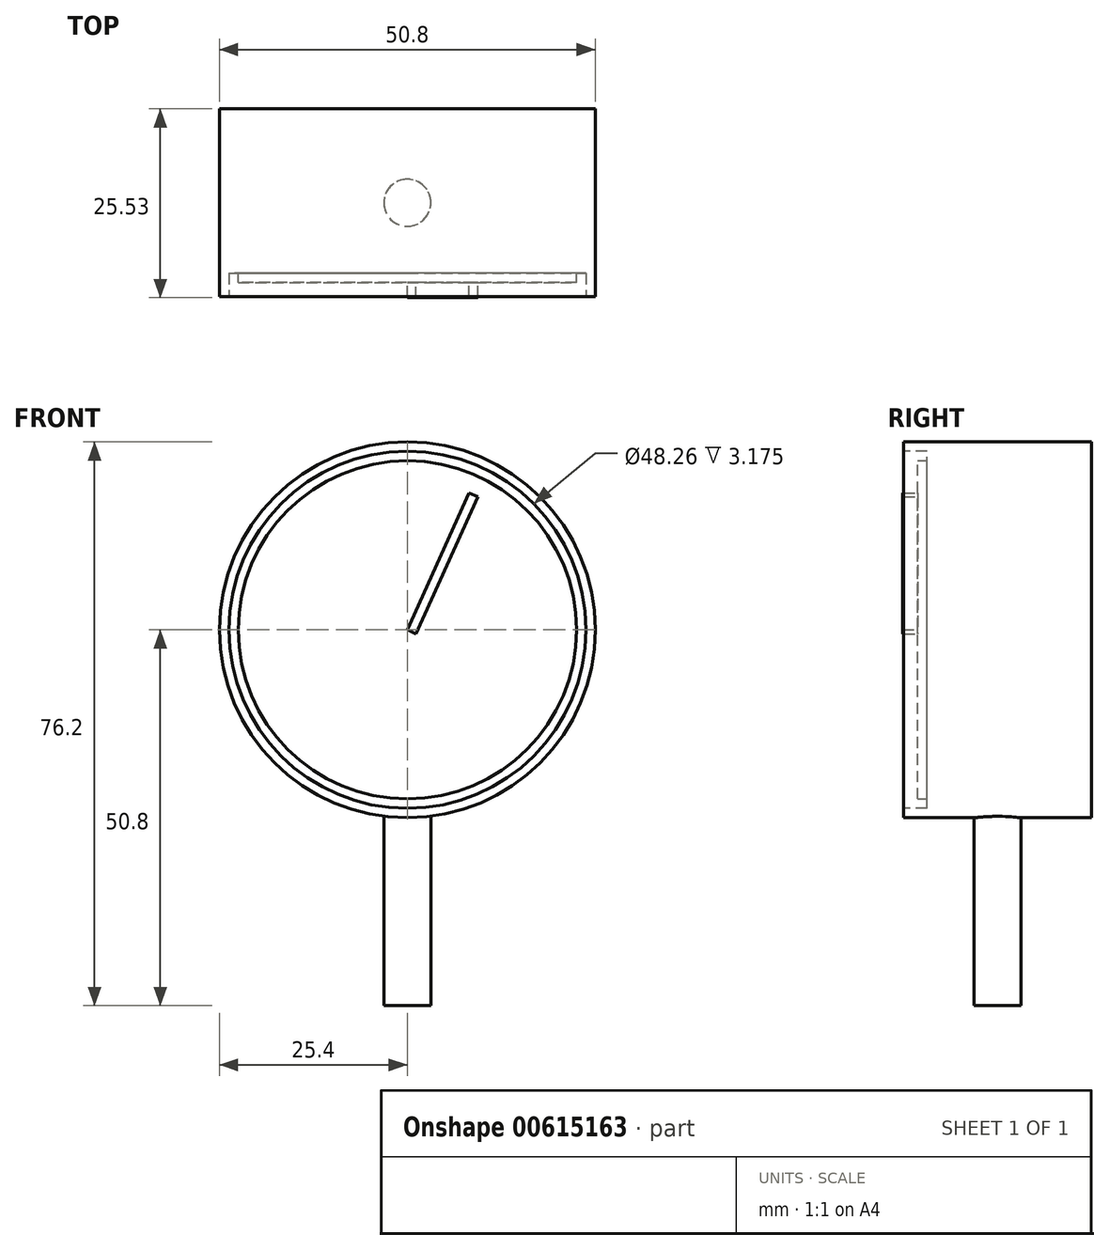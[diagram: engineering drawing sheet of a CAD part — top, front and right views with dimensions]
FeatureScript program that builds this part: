
annotation { "Feature Type Name" : "Feature", "Feature Type Description" : "" }
export const myFeature = defineFeature(function(context is Context, id is Id, definition is map)
    precondition{}
    {
        {
            var Q0;
            Q0=qCreatedBy(makeId("Front.planeOp"),FACE);
            var sketch = newSketch(context, id + "F0", { "sketchPlane" : qUnion([Q0])});
            skLineSegment(sketch, "E0", {"start": v(0, 0) * mm, "end": v(0, 38.1) * mm});
            skLineSegment(sketch, "E1", {"start": v(0, 38.1) * mm, "end": v(0, 50.8) * mm});
            skCircle(sketch, "E2", {"center": v(0, 50.8) * mm, "radius": 25.4 * mm});
            skSolve(sketch);
        }
        {
            var Q0;
            Q0=qCreatedBy(makeId("Top.planeOp"),FACE);
            var sketch = newSketch(context, id + "F1", { "sketchPlane" : qUnion([Q0])});
            skCircle(sketch, "E3", {"center": v(0, 0) * mm, "radius": 3.18 * mm});
            skSolve(sketch);
        }
        {
            var Q0;
            Q0 = qSketchRegion(id + "F1", true);
            extrude(context, id + "F2", {"entities" : qUnion([Q0]), "depth" : 38.1 * mm, "offsetDistance" : 25.4 * mm});
        }
        {
            var Q0;
            Q0 = qSketchRegion(id + "F0", true);
            extrude(context, id + "F3", {"entities" : qUnion([Q0]), "operationType" : NewBodyOperationType.ADD, "depth" : 25.4 * mm, "offsetDistance" : 25.4 * mm, "symmetric" : true});
        }
        {
            var Q0;
            Q0=makeQuery(id+"F3.opExtrude","CAP_FACE",FACE,{"disambiguationData":[OSD([sQuery(id+"F0.wireOp",EDGE,"E2")])],"isStart":false});
            var sketch = newSketch(context, id + "F4", { "sketchPlane" : qUnion([Q0])});
            skCircle(sketch, "E4", {"center": v(0, 50.8) * mm, "radius": 24.13 * mm});
            skSolve(sketch);
        }
        {
            var Q0;
            Q0 = qSketchRegion(id + "F4", true);
            extrude(context, id + "F5", {"entities" : qUnion([Q0]), "operationType" : NewBodyOperationType.ADD, "oppositeDirection" : true, "depth" : 3.17 * mm, "offsetDistance" : 25.4 * mm});
        }
        {
            var Q0;
            Q0=makeQuery(id+"F3.opExtrude","CAP_FACE",FACE,{"disambiguationData":[OSD([sQuery(id+"F0.wireOp",EDGE,"E2")])],"isStart":false});
            var sketch = newSketch(context, id + "F6", { "sketchPlane" : qUnion([Q0])});
            skCircle(sketch, "E5", {"center": v(0, 50.8) * mm, "radius": 24.13 * mm});
            skSolve(sketch);
        }
        {
            var Q0;
            Q0 = qSketchRegion(id + "F6", true);
            extrude(context, id + "F7", {"entities" : qUnion([Q0]), "operationType" : NewBodyOperationType.REMOVE, "oppositeDirection" : true, "depth" : 3.17 * mm, "offsetDistance" : 25.4 * mm});
        }
        {
            var Q0;
            Q0=makeQuery(id+"F7.boolean.opBoolean","COPY",FACE,{"derivedFrom":makeQuery(id+"F7.opExtrude","CAP_FACE",FACE,{"disambiguationData":[OSD([sQuery(id+"F6.wireOp",EDGE,"E5")])],"isStart":false})});
            var sketch = newSketch(context, id + "F8", { "sketchPlane" : qUnion([Q0])});
            skCircle(sketch, "E6", {"center": v(0, 50.8) * mm, "radius": 22.86 * mm});
            skSolve(sketch);
        }
        {
            var Q0;
            Q0 = qSketchRegion(id + "F8", true);
            extrude(context, id + "F9", {"entities" : qUnion([Q0]), "depth" : 1.27 * mm, "offsetDistance" : 25.4 * mm});
        }
        {
            var Q0;
            Q0=makeQuery(id+"F9.opExtrude","CAP_FACE",FACE,{"disambiguationData":[OSD([sQuery(id+"F8.wireOp",EDGE,"E6")])],"isStart":false});
            var sketch = newSketch(context, id + "F10", { "sketchPlane" : qUnion([Q0])});
            skLineSegment(sketch, "E7", {"start": v(0, 50.8) * mm, "end": v(8.35, 69.33) * mm});
            skLineSegment(sketch, "E8", {"start": v(8.35, 69.33) * mm, "end": v(9.5, 68.8) * mm});
            skLineSegment(sketch, "E9", {"start": v(9.5, 68.8) * mm, "end": v(1.16, 50.28) * mm});
            skLineSegment(sketch, "E10", {"start": v(1.16, 50.28) * mm, "end": v(0, 50.8) * mm});
            skSolve(sketch);
        }
        {
            var Q0;
            Q0 = qSketchRegion(id + "F10", true);
            extrude(context, id + "F11", {"entities" : qUnion([Q0]), "depth" : 2.03 * mm, "offsetDistance" : 25.4 * mm});
        }
    });
